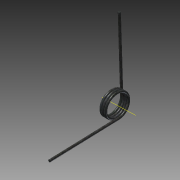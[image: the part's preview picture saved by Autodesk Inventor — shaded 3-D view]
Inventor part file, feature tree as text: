
AUTODESK INVENTOR PART (.ipt)
format: ipt  version: 2014 (Build 180170000, 170)  size: 217,600 bytes
history: native  units: in
note: dims shown in document units (in); Inventor stores cm internally (conversion verified against a paired STEP export)
features: other x3, plane x1, sketch x1, imported_body x1
ambient origin geometry x8: Origin, YZ Plane, XZ Plane, XY Plane, X Axis, Y Axis, Z Axis, Center Point
bodies: Body1 (feature_tree)
feature tree (6):
  parser-record x1  (decoder bookkeeping rows leaked as tree rows — omitted from the tree; the rows remain in map.json)
  other  "9271K5861"
  plane  "Work Plane1"
  sketch  "Sketch1"
  other  "Work Axis1"
  imported_body  "Base1"
